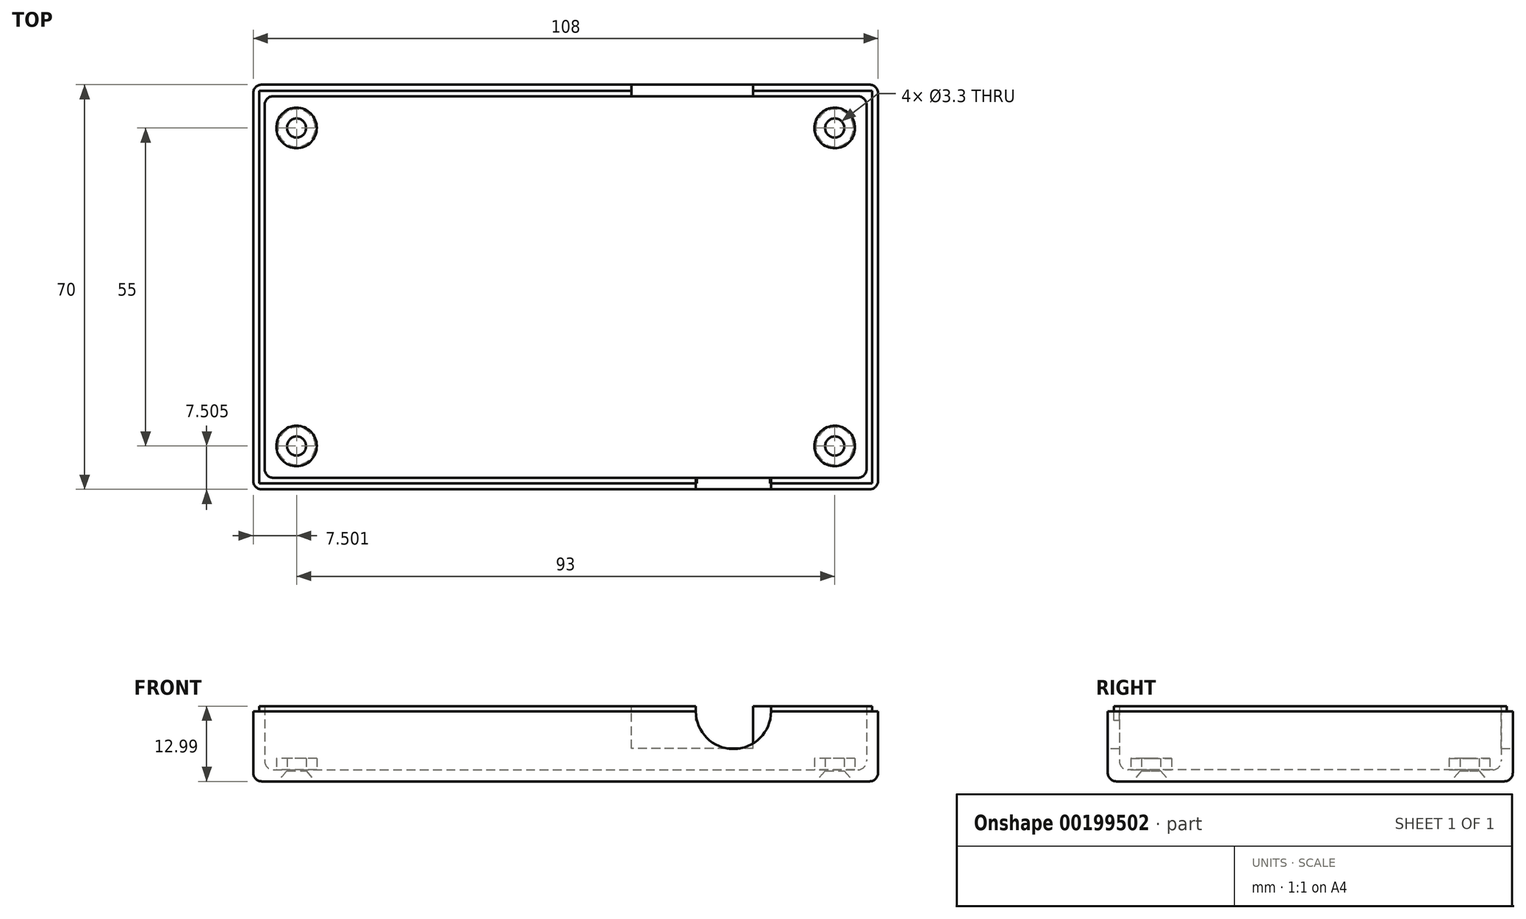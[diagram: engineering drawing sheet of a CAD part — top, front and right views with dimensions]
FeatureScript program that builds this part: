
annotation { "Feature Type Name" : "Feature", "Feature Type Description" : "" }
export const myFeature = defineFeature(function(context is Context, id is Id, definition is map)
    precondition{}
    {
        {
            var Q0;
            Q0=qCreatedBy(makeId("Top.planeOp"),FACE);
            var sketch = newSketch(context, id + "F0", { "sketchPlane" : qUnion([Q0])});
            skLineSegment(sketch, "E0.bottom", {"start": v(-44.36, 32.91) * mm, "end": v(63.64, 32.91) * mm});
            skLineSegment(sketch, "E0.top", {"start": v(-44.36, -37.09) * mm, "end": v(63.64, -37.09) * mm});
            skLineSegment(sketch, "E0.left", {"start": v(-44.36, 32.91) * mm, "end": v(-44.36, -37.09) * mm});
            skLineSegment(sketch, "E0.right", {"start": v(63.64, 32.91) * mm, "end": v(63.64, -37.09) * mm});
            skLineSegment(sketch, "E1.bottom", {"start": v(-43.3, 31.86) * mm, "end": v(62.6, 31.86) * mm});
            skLineSegment(sketch, "E1.top", {"start": v(-43.3, -36.04) * mm, "end": v(62.6, -36.04) * mm});
            skLineSegment(sketch, "E1.left", {"start": v(-43.3, 31.86) * mm, "end": v(-43.3, -36.04) * mm});
            skLineSegment(sketch, "E1.right", {"start": v(62.6, 31.86) * mm, "end": v(62.6, -36.04) * mm});
            skLineSegment(sketch, "E2.bottom", {"start": v(-42.36, 30.91) * mm, "end": v(61.64, 30.91) * mm});
            skLineSegment(sketch, "E2.top", {"start": v(-42.36, -35.09) * mm, "end": v(61.64, -35.09) * mm});
            skLineSegment(sketch, "E2.left", {"start": v(-42.36, 30.91) * mm, "end": v(-42.36, -35.09) * mm});
            skLineSegment(sketch, "E2.right", {"start": v(61.64, 30.91) * mm, "end": v(61.64, -35.09) * mm});
            skCircle(sketch, "E3", {"center": v(-36.86, 25.41) * mm, "radius": 3 * mm});
            skCircle(sketch, "E4", {"center": v(57.14, 25.41) * mm, "radius": 3 * mm});
            skCircle(sketch, "E5", {"center": v(54.92, -29.59) * mm, "radius": 3 * mm});
            skCircle(sketch, "E6", {"center": v(-36.86, -29.59) * mm, "radius": 3 * mm});
            skSolve(sketch);
        }
        {
            var Q0;
            Q0=makeQuery(id+"F0.imprint","IMPRINT",FACE,{"disambiguationData":[TD([[makeQuery(id+"F0.imprint","IMPRINT",EDGE,{"derivedFrom":sQuery(id+"F0.wireOp",EDGE,"E2.bottom")}),-1.0]])]});
            var Q1;
            Q1=makeQuery(id+"F0.imprint","IMPRINT",FACE,{"disambiguationData":[TD([[makeQuery(id+"F0.imprint","IMPRINT",EDGE,{"derivedFrom":sQuery(id+"F0.wireOp",EDGE,"E1.bottom")}),-1.0]])]});
            var Q2;
            Q2=makeQuery(id+"F0.imprint","IMPRINT",FACE,{"disambiguationData":[TD([[makeQuery(id+"F0.imprint","IMPRINT",EDGE,{"derivedFrom":sQuery(id+"F0.wireOp",EDGE,"E0.bottom")}),-1.0]])]});
            var Q3;
            Q3=makeQuery(id+"F0.imprint","IMPRINT",FACE,{"disambiguationData":[TD([[makeQuery(id+"F0.imprint","IMPRINT",EDGE,{"derivedFrom":sQuery(id+"F0.wireOp",EDGE,"E6")}),1.0]])]});
            var Q4;
            Q4=makeQuery(id+"F0.imprint","IMPRINT",FACE,{"disambiguationData":[TD([[makeQuery(id+"F0.imprint","IMPRINT",EDGE,{"derivedFrom":sQuery(id+"F0.wireOp",EDGE,"E5")}),1.0]])]});
            var Q5;
            Q5=makeQuery(id+"F0.imprint","IMPRINT",FACE,{"disambiguationData":[TD([[makeQuery(id+"F0.imprint","IMPRINT",EDGE,{"derivedFrom":sQuery(id+"F0.wireOp",EDGE,"E3")}),1.0]])]});
            var Q6;
            Q6=makeQuery(id+"F0.imprint","IMPRINT",FACE,{"disambiguationData":[TD([[makeQuery(id+"F0.imprint","IMPRINT",EDGE,{"derivedFrom":sQuery(id+"F0.wireOp",EDGE,"E4")}),1.0]])]});
            extrude(context, id + "F1", {"entities" : qUnion([Q0, Q1, Q2, Q3, Q4, Q5, Q6]), "oppositeDirection" : true, "depth" : 2 * mm});
        }
        {
            var Q0;
            Q0=makeQuery(id+"F0.imprint","IMPRINT",FACE,{"disambiguationData":[TD([[makeQuery(id+"F0.imprint","IMPRINT",EDGE,{"derivedFrom":sQuery(id+"F0.wireOp",EDGE,"E1.bottom")}),-1.0]])]});
            extrude(context, id + "F2", {"entities" : qUnion([Q0]), "operationType" : NewBodyOperationType.ADD, "depth" : 11 * mm});
        }
        {
            var Q0;
            Q0 = qSketchRegion(id + "F0", true);
            extrude(context, id + "F3", {"entities" : qUnion([Q0]), "operationType" : NewBodyOperationType.ADD, "depth" : 10.1 * mm});
        }
        {
            var Q0;
            Q0=makeQuery(id+"F2.boolean.opBoolean","SPLIT",FACE,{"disambiguationData":[TD([makeQuery(id+"F2.opExtrude","SWEPT_FACE",FACE,{"disambiguationData":[OSD([sQuery(id+"F0.wireOp",EDGE,"E2.bottom")])]})])],"derivedFrom":makeQuery(id+"F1.opExtrude","CAP_FACE",FACE,{"disambiguationData":[OSD([sQuery(id+"F0.wireOp",EDGE,"E0.bottom"),sQuery(id+"F0.wireOp",EDGE,"E0.top"),sQuery(id+"F0.wireOp",EDGE,"E0.left"),sQuery(id+"F0.wireOp",EDGE,"E0.right")])],"isStart":true})});
            var sketch = newSketch(context, id + "F4", { "sketchPlane" : qUnion([Q0])});
            skCircle(sketch, "E7", {"center": v(-36.86, 25.41) * mm, "radius": 3.5 * mm});
            skCircle(sketch, "E8", {"center": v(56.14, 25.41) * mm, "radius": 3.5 * mm});
            skCircle(sketch, "E9", {"center": v(-36.86, -29.59) * mm, "radius": 3.5 * mm});
            skCircle(sketch, "E10", {"center": v(56.14, -29.59) * mm, "radius": 3.5 * mm});
            skSolve(sketch);
        }
        {
            var Q0;
            Q0=makeQuery(id+"F4.imprint","IMPRINT",FACE,{"disambiguationData":[TD([[makeQuery(id+"F4.imprint","IMPRINT",EDGE,{"derivedFrom":sQuery(id+"F4.wireOp",EDGE,"E7")}),1.0]])]});
            var Q1;
            Q1=makeQuery(id+"F4.imprint","IMPRINT",FACE,{"disambiguationData":[TD([[makeQuery(id+"F4.imprint","IMPRINT",EDGE,{"derivedFrom":sQuery(id+"F4.wireOp",EDGE,"E8")}),1.0]])]});
            var Q2;
            Q2=makeQuery(id+"F4.imprint","IMPRINT",FACE,{"disambiguationData":[TD([[makeQuery(id+"F4.imprint","IMPRINT",EDGE,{"derivedFrom":sQuery(id+"F4.wireOp",EDGE,"E10")}),1.0]])]});
            var Q3;
            Q3=makeQuery(id+"F4.imprint","IMPRINT",FACE,{"disambiguationData":[TD([[makeQuery(id+"F4.imprint","IMPRINT",EDGE,{"derivedFrom":sQuery(id+"F4.wireOp",EDGE,"E9")}),1.0]])]});
            extrude(context, id + "F5", {"entities" : qUnion([Q0, Q1, Q2, Q3]), "operationType" : NewBodyOperationType.ADD, "depth" : 2 * mm});
        }
        {
            var Q0;
            Q0=makeQuery(id+"F1.opExtrude","CAP_FACE",FACE,{"disambiguationData":[OSD([sQuery(id+"F0.wireOp",EDGE,"E0.bottom"),sQuery(id+"F0.wireOp",EDGE,"E0.top"),sQuery(id+"F0.wireOp",EDGE,"E0.left"),sQuery(id+"F0.wireOp",EDGE,"E0.right")])],"isStart":false});
            var sketch = newSketch(context, id + "F6", { "sketchPlane" : qUnion([Q0])});
            skPoint(sketch, "E11", {"position": v(-36.86, 29.59) * mm});
            skPoint(sketch, "E12", {"position": v(-36.86, -25.41) * mm});
            skPoint(sketch, "E13", {"position": v(56.14, 29.59) * mm});
            skPoint(sketch, "E14", {"position": v(56.14, -25.41) * mm});
            skSolve(sketch);
        }
        {
            var Q0;
            Q0=sQuery(id+"F6.wireOp",VERTEX,"E11");
            var Q1;
            Q1=sQuery(id+"F6.wireOp",VERTEX,"E13");
            var Q2;
            Q2=sQuery(id+"F6.wireOp",VERTEX,"E14");
            var Q3;
            Q3=sQuery(id+"F6.wireOp",VERTEX,"E12");
            var Q4;
            Q4=makeQuery(id+"F1.opExtrude","SWEPT_BODY",BODY,{"disambiguationData":[OSD([sQuery(id+"F0.wireOp",EDGE,"E0.bottom"),sQuery(id+"F0.wireOp",EDGE,"E0.top"),sQuery(id+"F0.wireOp",EDGE,"E0.left"),sQuery(id+"F0.wireOp",EDGE,"E0.right")])]});
            hole(context, id + "F7", {"style" : HoleStyle.C_SINK, "endStyle" : HoleEndStyle.THROUGH, "holeDiameter" : 3.3 * mm, "cSinkDiameter" : 6.48 * mm, "cSinkAngle" : 82 * degree, "startFromSketch" : true, "locations" : qUnion([Q0, Q1, Q2, Q3]), "scope" : qUnion([Q4]), "tappedDepth" : 12 * mm, "tapClearance" : 3});
        }
        {
            var Q0;
            {var subQ0=sQuery(id+"F0.wireOp",EDGE,"E0.bottom");Q0=makeQuery(id+"F3.boolean.opBoolean","MERGE",FACE,{"derivedFrom":[makeQuery(id+"F1.opExtrude","SWEPT_FACE",FACE,{"disambiguationData":[OSD([subQ0])]}),makeQuery(id+"F3.opExtrude","SWEPT_FACE",FACE,{"disambiguationData":[OSD([subQ0])]})]});}
            var sketch = newSketch(context, id + "F8", { "sketchPlane" : qUnion([Q0])});
            skLineSegment(sketch, "E15.bottom", {"start": v(-42.04, 3.7) * mm, "end": v(-21.04, 3.7) * mm});
            skLineSegment(sketch, "E15.top", {"start": v(-42.04, 10.1) * mm, "end": v(-21.04, 10.1) * mm});
            skLineSegment(sketch, "E15.left", {"start": v(-42.04, 3.7) * mm, "end": v(-42.04, 10.1) * mm});
            skLineSegment(sketch, "E15.right", {"start": v(-21.04, 3.7) * mm, "end": v(-21.04, 10.1) * mm});
            skSolve(sketch);
        }
        {
            var Q0;
            Q0=makeQuery(id+"F8.imprint","IMPRINT",FACE,{"disambiguationData":[TD([[makeQuery(id+"F8.imprint","IMPRINT",EDGE,{"derivedFrom":sQuery(id+"F8.wireOp",EDGE,"E15.bottom")}),1.0]])]});
            extrude(context, id + "F9", {"entities" : qUnion([Q0]), "operationType" : NewBodyOperationType.REMOVE, "oppositeDirection" : true, "depth" : 2.5 * mm});
        }
        {
            var Q0;
            Q0=makeQuery(id+"F2.opExtrude","CAP_FACE",FACE,{"disambiguationData":[OSD([sQuery(id+"F0.wireOp",EDGE,"E1.bottom"),sQuery(id+"F0.wireOp",EDGE,"E1.top"),sQuery(id+"F0.wireOp",EDGE,"E1.left"),sQuery(id+"F0.wireOp",EDGE,"E1.right"),sQuery(id+"F0.wireOp",EDGE,"E2.bottom"),sQuery(id+"F0.wireOp",EDGE,"E2.top"),sQuery(id+"F0.wireOp",EDGE,"E2.left"),sQuery(id+"F0.wireOp",EDGE,"E2.right")])],"isStart":false});
            var sketch = newSketch(context, id + "F10", { "sketchPlane" : qUnion([Q0])});
            skLineSegment(sketch, "E16.bottom", {"start": v(32.14, -34.76) * mm, "end": v(45.14, -34.76) * mm});
            skLineSegment(sketch, "E16.top", {"start": v(32.14, -37.76) * mm, "end": v(45.14, -37.76) * mm});
            skLineSegment(sketch, "E16.left", {"start": v(32.14, -34.76) * mm, "end": v(32.14, -37.76) * mm});
            skLineSegment(sketch, "E16.right", {"start": v(45.14, -34.76) * mm, "end": v(45.14, -37.76) * mm});
            skLineSegment(sketch, "E17.bottom", {"start": v(21.04, 33.86) * mm, "end": v(42.04, 33.86) * mm});
            skLineSegment(sketch, "E17.top", {"start": v(21.04, 28.86) * mm, "end": v(42.04, 28.86) * mm});
            skLineSegment(sketch, "E17.left", {"start": v(21.04, 33.86) * mm, "end": v(21.04, 28.86) * mm});
            skLineSegment(sketch, "E17.right", {"start": v(42.04, 33.86) * mm, "end": v(42.04, 28.86) * mm});
            skSolve(sketch);
        }
        {
            var Q0;
            {var subQ0=sQuery(id+"F10.wireOp",EDGE,"GH5rCHhh-geM3-sB2K-jFEz-GMiepMDtVWYR.bottom");Q0=makeQuery(id+"F10.imprint","IMPRINT",FACE,{"disambiguationData":[TD([[makeQuery(id+"F10.imprint","IMPRINT",EDGE,{"derivedFrom":subQ0}),-1.0]])]});}
            var Q1;
            {var subQ0=sQuery(id+"F10.wireOp",EDGE,"E16.left");var subQ1=makeQuery(id+"F2.opExtrude","CAP_EDGE",EDGE,{"disambiguationData":[OSD([sQuery(id+"F0.wireOp",EDGE,"E1.top")])],"isStart":false});var subQ2=makeQuery(id+"F10.imprint","INTERSECT",VERTEX,{"derivedFrom":[subQ1,subQ0]});Q1=makeQuery(id+"F10.imprint","IMPRINT",FACE,{"disambiguationData":[TD([[makeQuery(id+"F10.imprint","IMPRINT",EDGE,{"disambiguationData":[TD([[subQ2,1.0]])],"derivedFrom":subQ0}),1.0]])]});}
            extrude(context, id + "F11", {"entities" : qUnion([Q0, Q1]), "operationType" : NewBodyOperationType.REMOVE, "oppositeDirection" : true, "depth" : 2.5 * mm});
        }
        {
            var Q0;
            {var subQ0=sQuery(id+"F0.wireOp",EDGE,"E0.top");Q0=makeQuery(id+"F3.boolean.opBoolean","MERGE",FACE,{"derivedFrom":[makeQuery(id+"F1.opExtrude","SWEPT_FACE",FACE,{"disambiguationData":[OSD([subQ0])]}),makeQuery(id+"F3.opExtrude","SWEPT_FACE",FACE,{"disambiguationData":[OSD([subQ0])]})]});}
            var sketch = newSketch(context, id + "F12", { "sketchPlane" : qUnion([Q0])});
            skPoint(sketch, "E18", {"position": v(38.64, 10.1) * mm});
            skCircle(sketch, "E19", {"center": v(38.64, 10.1) * mm, "radius": 6.5 * mm});
            skSolve(sketch);
        }
        {
            var Q0;
            {var subQ0=sQuery(id+"F12.wireOp",EDGE,"E19");var subQ1=makeQuery(id+"F3.opExtrude","CAP_EDGE",EDGE,{"disambiguationData":[OSD([sQuery(id+"F0.wireOp",EDGE,"E0.top")])],"isStart":false});var subQ2=makeQuery(id+"F12.imprint","INTERSECT",VERTEX,{"disambiguationData":[OD(0.0)],"derivedFrom":[subQ1,subQ0]});Q0=makeQuery(id+"F12.imprint","IMPRINT",FACE,{"disambiguationData":[TD([[makeQuery(id+"F12.imprint","IMPRINT",EDGE,{"disambiguationData":[TD([[subQ2,-1.0]])],"derivedFrom":subQ0}),1.0]])]});}
            extrude(context, id + "F13", {"entities" : qUnion([Q0]), "operationType" : NewBodyOperationType.REMOVE, "oppositeDirection" : true, "depth" : 2.5 * mm});
        }
        {
            var Q0;
            {var subQ0=sQuery(id+"F0.wireOp",EDGE,"E0.right");var subQ1=sQuery(id+"F0.wireOp",EDGE,"E0.top");Q0=makeQuery(id+"F3.boolean.opBoolean","MERGE",EDGE,{"derivedFrom":[makeQuery(id+"F1.opExtrude","SWEPT_EDGE",EDGE,{"disambiguationData":[OSD([subQ1,subQ0])]}),makeQuery(id+"F3.opExtrude","SWEPT_EDGE",EDGE,{"disambiguationData":[OSD([subQ1,subQ0])]})]});}
            var Q1;
            Q1=makeQuery(id+"F1.opExtrude","CAP_EDGE",EDGE,{"disambiguationData":[OSD([sQuery(id+"F0.wireOp",EDGE,"E0.right")])],"isStart":false});
            var Q2;
            {var subQ0=sQuery(id+"F0.wireOp",EDGE,"E0.right");var subQ1=sQuery(id+"F0.wireOp",EDGE,"E0.bottom");Q2=makeQuery(id+"F3.boolean.opBoolean","MERGE",EDGE,{"derivedFrom":[makeQuery(id+"F1.opExtrude","SWEPT_EDGE",EDGE,{"disambiguationData":[OSD([subQ1,subQ0])]}),makeQuery(id+"F3.opExtrude","SWEPT_EDGE",EDGE,{"disambiguationData":[OSD([subQ1,subQ0])]})]});}
            var Q3;
            Q3=makeQuery(id+"F1.opExtrude","CAP_EDGE",EDGE,{"disambiguationData":[OSD([sQuery(id+"F0.wireOp",EDGE,"E0.bottom")])],"isStart":false});
            var Q4;
            {var subQ0=sQuery(id+"F0.wireOp",EDGE,"E0.left");var subQ1=sQuery(id+"F0.wireOp",EDGE,"E0.bottom");Q4=makeQuery(id+"F3.boolean.opBoolean","MERGE",EDGE,{"derivedFrom":[makeQuery(id+"F1.opExtrude","SWEPT_EDGE",EDGE,{"disambiguationData":[OSD([subQ1,subQ0])]}),makeQuery(id+"F3.opExtrude","SWEPT_EDGE",EDGE,{"disambiguationData":[OSD([subQ1,subQ0])]})]});}
            var Q5;
            {var subQ0=sQuery(id+"F0.wireOp",EDGE,"E0.left");var subQ1=sQuery(id+"F0.wireOp",EDGE,"E0.top");Q5=makeQuery(id+"F3.boolean.opBoolean","MERGE",EDGE,{"derivedFrom":[makeQuery(id+"F1.opExtrude","SWEPT_EDGE",EDGE,{"disambiguationData":[OSD([subQ1,subQ0])]}),makeQuery(id+"F3.opExtrude","SWEPT_EDGE",EDGE,{"disambiguationData":[OSD([subQ1,subQ0])]})]});}
            var Q6;
            Q6=makeQuery(id+"F1.opExtrude","CAP_EDGE",EDGE,{"disambiguationData":[OSD([sQuery(id+"F0.wireOp",EDGE,"E0.left")])],"isStart":false});
            var Q7;
            Q7=makeQuery(id+"F1.opExtrude","CAP_EDGE",EDGE,{"disambiguationData":[OSD([sQuery(id+"F0.wireOp",EDGE,"E0.top")])],"isStart":false});
            fillet(context, id + "F14", {"entities" : qUnion([Q0, Q1, Q2, Q3, Q4, Q5, Q6, Q7]), "radius" : 1.5 * mm, "tangentPropagation" : true, "allowEdgeOverflow" : false});
        }
        {
            var Q0;
            Q0=makeQuery(id+"F2.opExtrude","CAP_EDGE",EDGE,{"disambiguationData":[OSD([sQuery(id+"F0.wireOp",EDGE,"E2.bottom")])],"isStart":true});
            var Q1;
            Q1=makeQuery(id+"F2.opExtrude","SWEPT_EDGE",EDGE,{"disambiguationData":[OSD([sQuery(id+"F0.wireOp",EDGE,"E2.bottom"),sQuery(id+"F0.wireOp",EDGE,"E2.left")])]});
            var Q2;
            Q2=makeQuery(id+"F2.opExtrude","CAP_EDGE",EDGE,{"disambiguationData":[OSD([sQuery(id+"F0.wireOp",EDGE,"E2.left")])],"isStart":true});
            var Q3;
            Q3=makeQuery(id+"F2.opExtrude","CAP_EDGE",EDGE,{"disambiguationData":[OSD([sQuery(id+"F0.wireOp",EDGE,"E2.top")])],"isStart":true});
            var Q4;
            Q4=makeQuery(id+"F2.opExtrude","SWEPT_EDGE",EDGE,{"disambiguationData":[OSD([sQuery(id+"F0.wireOp",EDGE,"E2.top"),sQuery(id+"F0.wireOp",EDGE,"E2.left")])]});
            var Q5;
            Q5=makeQuery(id+"F2.opExtrude","SWEPT_EDGE",EDGE,{"disambiguationData":[OSD([sQuery(id+"F0.wireOp",EDGE,"E2.bottom"),sQuery(id+"F0.wireOp",EDGE,"E2.right")])]});
            var Q6;
            Q6=makeQuery(id+"F2.opExtrude","CAP_EDGE",EDGE,{"disambiguationData":[OSD([sQuery(id+"F0.wireOp",EDGE,"E2.right")])],"isStart":true});
            var Q7;
            Q7=makeQuery(id+"F2.opExtrude","SWEPT_EDGE",EDGE,{"disambiguationData":[OSD([sQuery(id+"F0.wireOp",EDGE,"E2.top"),sQuery(id+"F0.wireOp",EDGE,"E2.right")])]});
            fillet(context, id + "F15", {"entities" : qUnion([Q0, Q1, Q2, Q3, Q4, Q5, Q6, Q7]), "radius" : 1.5 * mm, "tangentPropagation" : true, "allowEdgeOverflow" : false});
        }
        {
            var Q0;
            Q0=makeQuery(id+"F2.opExtrude","SWEPT_FACE",FACE,{"disambiguationData":[OSD([sQuery(id+"F0.wireOp",EDGE,"E1.bottom")])]});
            var sketch = newSketch(context, id + "F16", { "sketchPlane" : qUnion([Q0])});
            skLineSegment(sketch, "E20.bottom", {"start": v(-21.04, 10.1) * mm, "end": v(-42.04, 10.1) * mm});
            skLineSegment(sketch, "E20.top", {"start": v(-21.04, 11) * mm, "end": v(-42.04, 11) * mm});
            skLineSegment(sketch, "E20.left", {"start": v(-21.04, 10.1) * mm, "end": v(-21.04, 11) * mm});
            skLineSegment(sketch, "E20.right", {"start": v(-42.04, 10.1) * mm, "end": v(-42.04, 11) * mm});
            skSolve(sketch);
        }
        {
            var Q0;
            Q0=makeQuery(id+"F16.imprint","IMPRINT",FACE,{"disambiguationData":[TD([[makeQuery(id+"F16.imprint","IMPRINT",EDGE,{"derivedFrom":sQuery(id+"F16.wireOp",EDGE,"E20.bottom")}),-1.0]])]});
            extrude(context, id + "F17", {"entities" : qUnion([Q0]), "operationType" : NewBodyOperationType.REMOVE, "oppositeDirection" : true, "depth" : 2.5 * mm});
        }
    });
